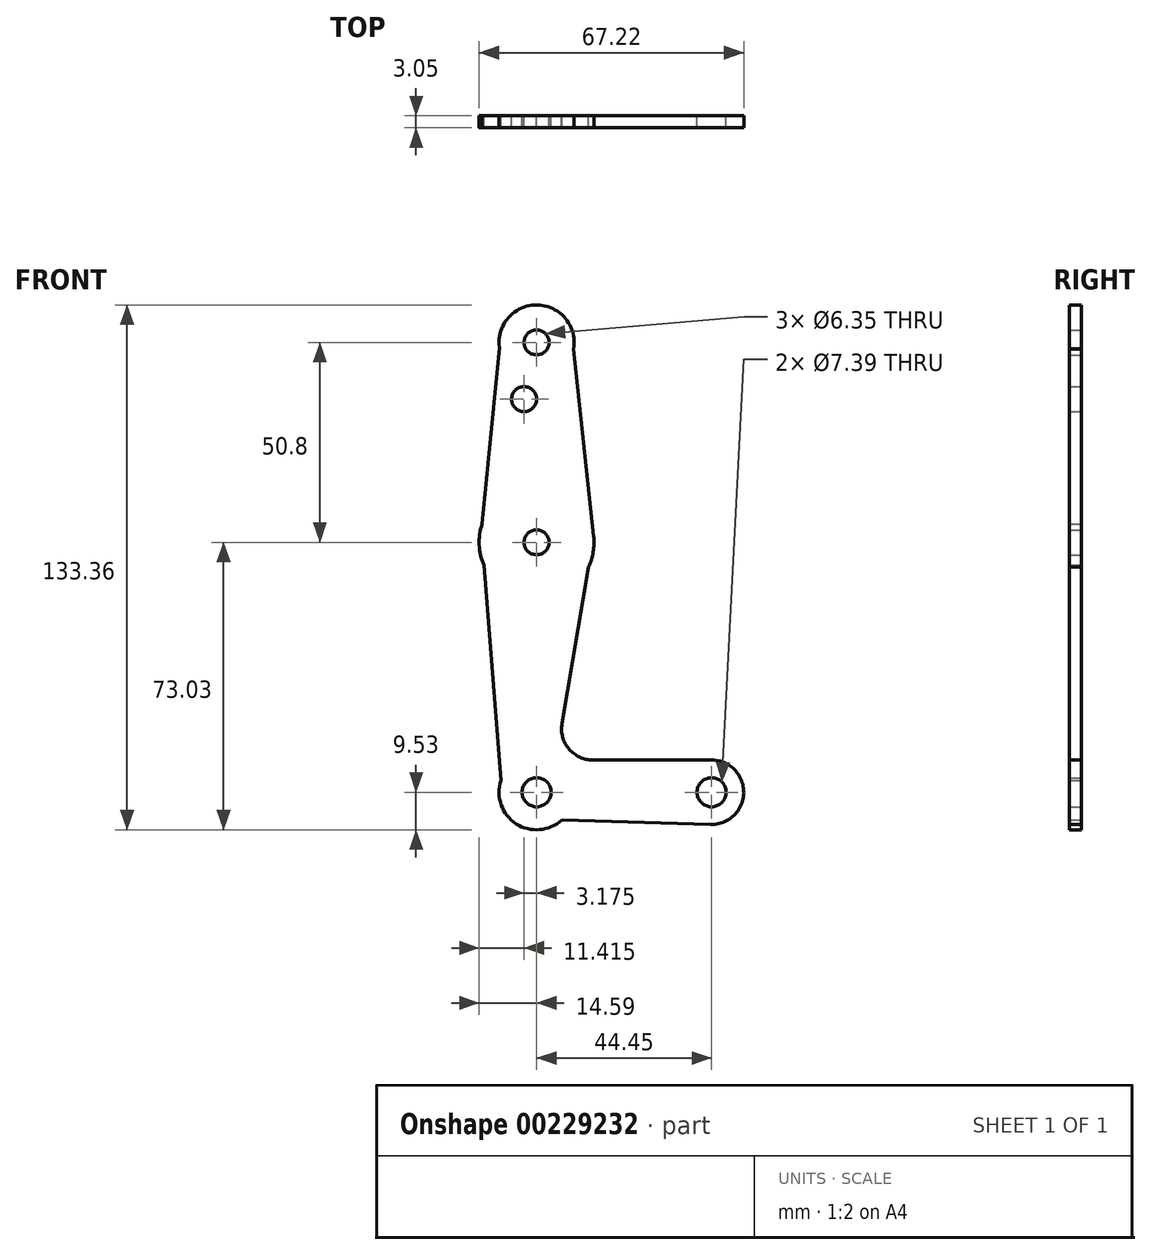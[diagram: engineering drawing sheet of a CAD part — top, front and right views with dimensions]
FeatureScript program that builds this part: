
annotation { "Feature Type Name" : "Feature", "Feature Type Description" : "" }
export const myFeature = defineFeature(function(context is Context, id is Id, definition is map)
    precondition{}
    {
        {
            var Q0;
            Q0=qCreatedBy(makeId("Front.planeOp"),FACE);
            var sketch = newSketch(context, id + "F0", { "sketchPlane" : qUnion([Q0])});
            skCircle(sketch, "E0", {"center": v(0, 114.3) * mm, "radius": 9.53 * mm});
            skCircle(sketch, "E1", {"center": v(0, 0) * mm, "radius": 9.53 * mm});
            skCircle(sketch, "E2", {"center": v(0, 63.5) * mm, "radius": 14.6 * mm});
            skCircle(sketch, "E3", {"center": v(44.45, 0) * mm, "radius": 8.18 * mm});
            skPoint(sketch, "E4.newPointA", {"position": v(0, 9.53) * mm});
            skPoint(sketch, "E4.newPointB", {"position": v(9.55, 0) * mm});
            skCircle(sketch, "E5", {"center": v(0, 114.3) * mm, "radius": 3.18 * mm});
            skCircle(sketch, "E6", {"center": v(0, 63.5) * mm, "radius": 3.18 * mm});
            skCircle(sketch, "E7", {"center": v(0, 0) * mm, "radius": 3.7 * mm});
            skCircle(sketch, "E8", {"center": v(44.45, 0) * mm, "radius": 3.7 * mm});
            skCircle(sketch, "E9", {"center": v(-3.18, 99.89) * mm, "radius": 3.18 * mm});
            skLineSegment(sketch, "E10", {"start": v(-9.44, 113) * mm, "end": v(-13.84, 68.13) * mm});
            skLineSegment(sketch, "E11", {"start": v(-14.15, 67.07) * mm, "end": v(-9.05, 2.98) * mm});
            skLineSegment(sketch, "E12", {"start": v(6.42, -7.03) * mm, "end": v(44.2, -8.17) * mm});
            skLineSegment(sketch, "E13", {"start": v(44.45, 8.18) * mm, "end": v(14.3, 8.18) * mm});
            skLineSegment(sketch, "E14", {"start": v(6.45, 17.45) * mm, "end": v(14.51, 65.06) * mm});
            skLineSegment(sketch, "E15", {"start": v(14.51, 65.06) * mm, "end": v(9.38, 112.66) * mm});
            skPoint(sketch, "E16.visualSharp", {"position": v(4.88, 8.18) * mm});
            skArc(sketch, "E16.filletArc", {"start": v(6.45, 17.45) * mm, "mid": v(8.22, 11) * mm, "end": v(14.3, 8.18) * mm});
            skSolve(sketch);
        }
        {
            var Q0;
            Q0 = qSketchRegion(id + "F0", true);
            extrude(context, id + "F1", {"entities" : qUnion([Q0]), "depth" : 3.05 * mm});
        }
        {
            var Q0;
            Q0=sQuery(id+"F0.wireOp",EDGE,"E2");
            var Q1;
            Q1=sQuery(id+"F0.wireOp",EDGE,"E6");
            extrude(context, id + "F2", {"bodyType" : ToolBodyType.SURFACE, "surfaceEntities" : qUnion([Q0, Q1]), "endBound" : BoundingType.SYMMETRIC, "oppositeDirection" : true, "depth" : 50.8 * mm, "hasSecondDirection" : true, "secondDirectionOppositeDirection" : false, "secondDirectionDepth" : 25.4 * mm});
        }
        {
            var Q0;
            Q0=sQuery(id+"F0.wireOp",EDGE,"E0");
            var Q1;
            Q1=sQuery(id+"F0.wireOp",EDGE,"E3");
            var Q2;
            Q2=sQuery(id+"F0.wireOp",EDGE,"E5");
            var Q3;
            Q3=sQuery(id+"F0.wireOp",EDGE,"E8");
            extrude(context, id + "F3", {"bodyType" : ToolBodyType.SURFACE, "surfaceEntities" : qUnion([Q0, Q1, Q2, Q3]), "endBound" : BoundingType.SYMMETRIC, "depth" : 25.4 * mm});
        }
    });
